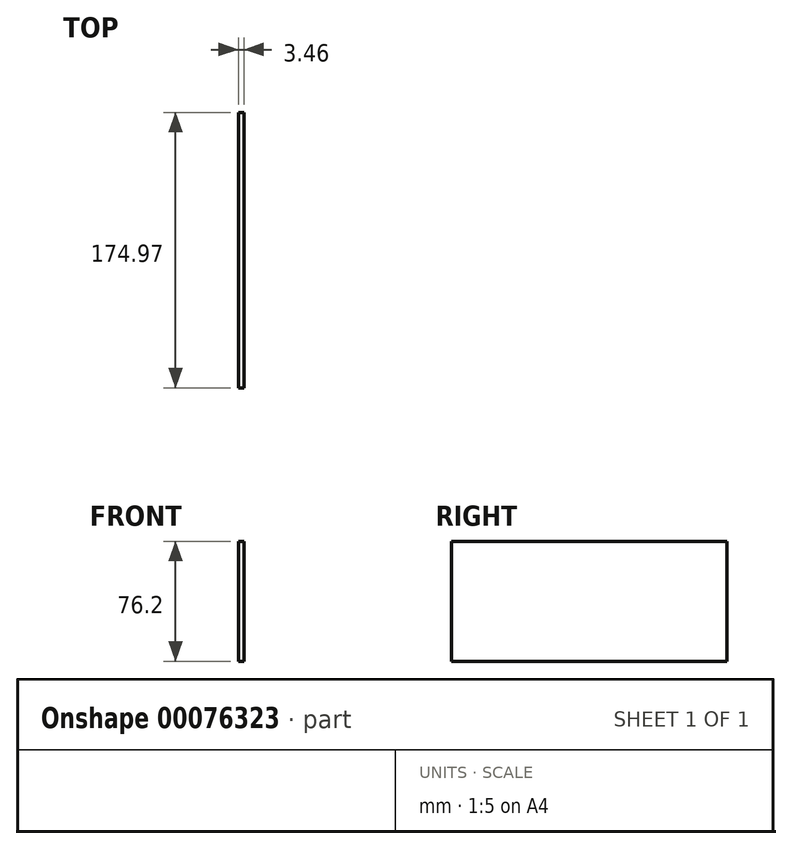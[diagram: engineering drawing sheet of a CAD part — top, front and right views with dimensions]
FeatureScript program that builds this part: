
annotation { "Feature Type Name" : "Feature", "Feature Type Description" : "" }
export const myFeature = defineFeature(function(context is Context, id is Id, definition is map)
    precondition{}
    {
        {
            var Q0;
            Q0=qCreatedBy(makeId("Top.planeOp"),FACE);
            var sketch = newSketch(context, id + "F0", { "sketchPlane" : qUnion([Q0])});
            skLineSegment(sketch, "E0.bottom", {"start": v(-69.92, 69.34) * mm, "end": v(-15.66, 69.34) * mm});
            skLineSegment(sketch, "E0.top", {"start": v(-69.92, -29.43) * mm, "end": v(-15.66, -29.43) * mm});
            skLineSegment(sketch, "E0.left", {"start": v(-69.92, 69.34) * mm, "end": v(-69.92, -29.43) * mm});
            skLineSegment(sketch, "E0.right", {"start": v(-15.66, 69.34) * mm, "end": v(-15.66, -29.43) * mm});
            skSolve(sketch);
        }
        {
            var Q0;
            Q0=makeQuery(id+"F0.imprint","IMPRINT",FACE,{"disambiguationData":[TD([[makeQuery(id+"F0.imprint","IMPRINT",EDGE,{"derivedFrom":sQuery(id+"F0.wireOp",EDGE,"E0.bottom")}),-1.0]])]});
            extrude(context, id + "F1", {"entities" : qUnion([Q0]), "depth" : 76.2 * mm});
        }
        {
            var Q0;
            Q0=makeQuery(id+"F1.opExtrude","SWEPT_FACE",FACE,{"disambiguationData":[OSD([sQuery(id+"F0.wireOp",EDGE,"E0.right")])]});
            extrude(context, id + "F2", {"entities" : qUnion([Q0]), "operationType" : NewBodyOperationType.REMOVE, "oppositeDirection" : true, "depth" : 25.4 * mm});
        }
        {
            var Q0;
            Q0=makeQuery(id+"F2.boolean.opBoolean","COPY",FACE,{"derivedFrom":makeQuery(id+"F2.opExtrude","CAP_FACE",FACE,{"disambiguationData":[OSD([sQuery(id+"F0.wireOp",EDGE,"E0.right")])],"isStart":false})});
            extrude(context, id + "F3", {"entities" : qUnion([Q0]), "operationType" : NewBodyOperationType.REMOVE, "oppositeDirection" : true, "depth" : 25.4 * mm});
        }
        {
            var Q0;
            Q0=makeQuery(id+"F1.opExtrude","SWEPT_FACE",FACE,{"disambiguationData":[OSD([sQuery(id+"F0.wireOp",EDGE,"E0.top")])]});
            extrude(context, id + "F4", {"entities" : qUnion([Q0]), "operationType" : NewBodyOperationType.ADD, "depth" : 76.2 * mm});
        }
    });
